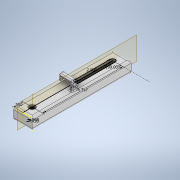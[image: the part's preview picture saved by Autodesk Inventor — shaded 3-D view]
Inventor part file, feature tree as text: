
AUTODESK INVENTOR PART (.ipt)
format: ipt  version: 2020 (Build 240168000, 168)  size: 236,032 bytes
history: native  units: in
note: dims shown in document units (in); Inventor stores cm internally (conversion verified against a paired STEP export)
features: sketch x6, extrude x5, hole x2, fillet x2, plane x1, other x1, revolve x1
ambient origin geometry x8: Origin, YZ Plane, XZ Plane, XY Plane, X Axis, Y Axis, Z Axis, Center Point
bodies: Solid1 (feature_tree)
feature tree (18):
  extrude  "Extrusion1"  Depth=5.357in
  sketch  "Sketch2"  dims[d2=0.625in d3=0.0in d4=0.5in d5=4.357in]
  hole  "Hole1"  [1 undecoded]
  fillet  "Fillet1"  Radius=4.357in
  extrude  "Extrusion2"  Depth=0.125in
  extrude  "Extrusion3"  TaperAngle=0.0deg  [1 undecoded]
  fillet  "Fillet2"  Radius=0.125in
  hole  "Hole2"  [1 undecoded]
  extrude  "Extrusion4"  TaperAngle=135.0deg  [1 undecoded]
  sketch  "Sketch6"  dims[d17=0.25in d18=0.5in d19=0.0in]
  extrude  "Extrusion5"  Depth=0.5in TaperAngle=0.0deg
  plane  "Work Plane1"
  other  "Work Axis2"
  revolve  "Revolution1"  [1 undecoded]
  sketch  "Sketch1"  dims[d0=1.0in d1=5.357in]
  sketch  "Sketch3"  dims[d6=0.266in d7=0.5in d8=0.438in d9=0.25in d10=0.5635in d11=0.75in d12=0.8108in d13=0.125in]
  sketch  "Sketch4"  dims[d14=2.3035in d15=0.0in d16=0.125in]
  sketch  "Sketch8"  dims[d20=0.2in d21=135.0deg d22=0.5in d23=0.0in d24=0.0625in d25=0.332in d26=0.75in d27=0.531in d28=0.313in d29=0.5635in d30=1.0in d31=0.8108in d32=2.0in d33=90.0deg d34=0.26in d35=0.5in d36=0.0in d39=0.43in d40=0.5in d41=0.5in d42=0.0in d48=0.25in d49=0.0in d50=0.0687in]
note: 5 required parameter values undecoded (feature->parameter linkage not recoverable at this tier; creation-order binding heuristic only, values carry confidence <= 0.55)